# Revit family: sipario_o_73_mm_273a
name_source: partatom
category: Lighting Fixtures
units: mm (PartAtom-declared; Revit-internal decimal feet)

## family parameters
Cut with Voids When Loaded = No
Host = Face
Light Source = No
Part Type = Normal
Room Calculation Point = No
Round Connector Dimension = Use Diameter
Shared = No

## types (1)
- Sipario ø 73 mm (1 x LED, 2430 lm, 4000K)
    Apparent Load = 21 VA
    CIE Flux Codes = 100 100 100 100 87
    Color Rendering = 90
    Color Temperature = 4000K
    Default Elevation = 1800 mm
    Description = 273A : 
Ø73 adjustable spotlight with adapter for installation on a base or electrified track. LED lamp with C.O.B. (Chip on board) technology, -CRI90- high colour rendering and 4000K tone.  
Die-cast aluminium body with thermoplastic rear cap and front ring (Mass-Balance). The product can be rotated by 360° around the vertical axis with a mechanical lock and tilted by 90° relative to the horizontal plane. Passive heat dissipation.  
OptiBeam Reflector optical system with Medium optic. Anti-scratch reflector made of P.V.D. (Physical Vapour Deposition) aluminium that can provide optimum performance in terms of light efficiency.  
Dimmable electronic DALI-2 power supply integrated in the body of the luminaire.  
Body complete with dimmable power supply unit and Casambi protocol positioned inside the product track adapter. The components used allow the products to be controlled with the Casambi system app and components, enabling on-off, dimming and scene recall functions and allowing multiple luminaires to operate in a Casambi mesh network. 2.4 GHz bluetooth frequency. The app is available on the Apple Store and Google Play Store. Integrated Beacon that can be activated via an app (iBeacon) that enables smart functions for third party applications and the Jiminy Push Notification app.  
Spotlight with Push & Go system designed to facilitate and safely accelerate the connection between product and optic accessory. Mechanically disconnecting the accessory allows it to be disengaged but not dropped. Three internal accessories and one external one can be used simultaneously. All internal accessories rotate 360° about the spotlight longitudinal axis.


273A.01 - SIPARIO Ø73 spotlight - CASAMBI   - Medium - OBReflector - - 21.2W 2114.1lm - 4000K - CRI 90 - White
H15W - Lamp LED 4000K CRI90
    Height = 164 mm
    Lamp = 1 x LED
    Lamp Light Flux = 2430 lm
    Lamp count = 1
    Length = 73 mm
    Lifetime = 100000 h
    Luminous efficacy = 100 lm/W
    Manufacturer = iGuzzini
    ModVariant = No
    Model = 273A
    Number of Poles = 1
    OnlyDefault = Yes
    Power Factor = 1
    Product Name = Sipario ø 73 mm
    Product group = track mounted spotlight
    ProductGroupID = 12
    Protection Class = Protection class
    Protection Degree = Degree of protection
    RLX_Detail_Level = 1
    RLX_Emergency_Light_Flux = 0 lm
    RLX_Emergency_Type = 0
    RLX_Emergency_Type_DB = No
    RlxData = <blob elided: 29417 chars, md5=288db1ad>
    Socket = socket
    Standby Power = 0 W
    System Light Flux = 2114 lm
    System Power = 21 W
    Type Comments = Product without accessories
    Type Image = sipario-73_riflettore_nero_img0015099_thum.jpg
    URL = http://relux.com
    VarID = ---
    Voltage = 0 V
    Weight = 0.00 kg
    Width = 0 mm  [stored 0 ft]

note: [stored X ft] marks values corroborated as IEEE doubles in the binary element streams (Revit-internal decimal feet)

## geometry (parser evidence)
native form markers: Blend x4, Sweep x14
no freeform markers — native parametric forms only
